# Revit family: Door-Industrial_Door-Dynaco-M2_Freezer
name_source: partatom
category: Doors
revit_build: Autodesk Revit 2016 (Build: 20150714_1515(x64)
units: mm (PartAtom-declared; Revit-internal decimal feet)

## family parameters
Always vertical = Yes
Cut with Voids When Loaded = No
Host = Wall
Room Calculation Point = No
Shared = No

## types (1)
- Dynaco_M2_Freezer
    Air permeability, EN 12426 = class 1 ,(24 m3/m2/h at 50 Pa)
/m2
/h at 50 Pa)
    Analytic Construction = <None>
    BIMobject category = Industrial Doors
    C1 = Yes
    C2 = Yes
    C3 = Yes
    C4 = Yes
    Closing Speed = 1,2 m/s
    Control unit Distance = 600 mm
    Control unit Height = 1500 mm  [stored 4.92126 ft]
    Date of publishing = 2015-10-01
    Depth = 0.00
    Design country = Belgium
    Edition number = 1
    Four Column Windows = Yes
    IFC Classification = Door
    Lifetime expectations = 1.000.000 cycles
    Manufacturer country = Belgium
    Manufacturer name = Entrematic
    Material main = PVC
    Material secondary = Steel
    NBS Reference Code = 59-23-38
    NBS Reference Description = High Speed Doorsets
    Nominal height = 550000
    Nominal width = 400000
    One Column Windows = Yes
    Opening Speed = up to 2,4 m/s 2
    Option 1 = Stainless steel
    Product Guid = 524e091b-e548-4cc9-bef3-8e8686cbfe03
    Product SKU = dyn-m2-fr
    Product data url = http://bimobject.com
    Product family = High speed door
    Product group = Freezer door
    QR code = http://bimobject.com
    Technical description = https://www.dynacodoor.com
    Thermal transmittance = 6,02 W/ (m2 K)
K)
    Three Column Windows = Yes
    Two Column Windows = Yes
    UNSPSC Code = 301715
    Uniclass 1.4 Code = L411
    Uniclass 1.4 Description = Doors
    Uniclass 2.0 Code = PR-59-23-38
    Uniclass 2.0 Description = High Speed Doorsets
    Unit box = Dynalogic 2 - 380mm x 380mm
    Water penetration, EN 12425 = class 1 (30 N/m2)
)
    Weight Net (Kg) = 0
    Wind load resistance, EN 12424 = class 1 (300 N/m2)
)

note: [stored X ft] marks values corroborated as IEEE doubles in the binary element streams (Revit-internal decimal feet)

## geometry (parser evidence)
native form markers: Blend x6, Sweep x19
no freeform markers — native parametric forms only
